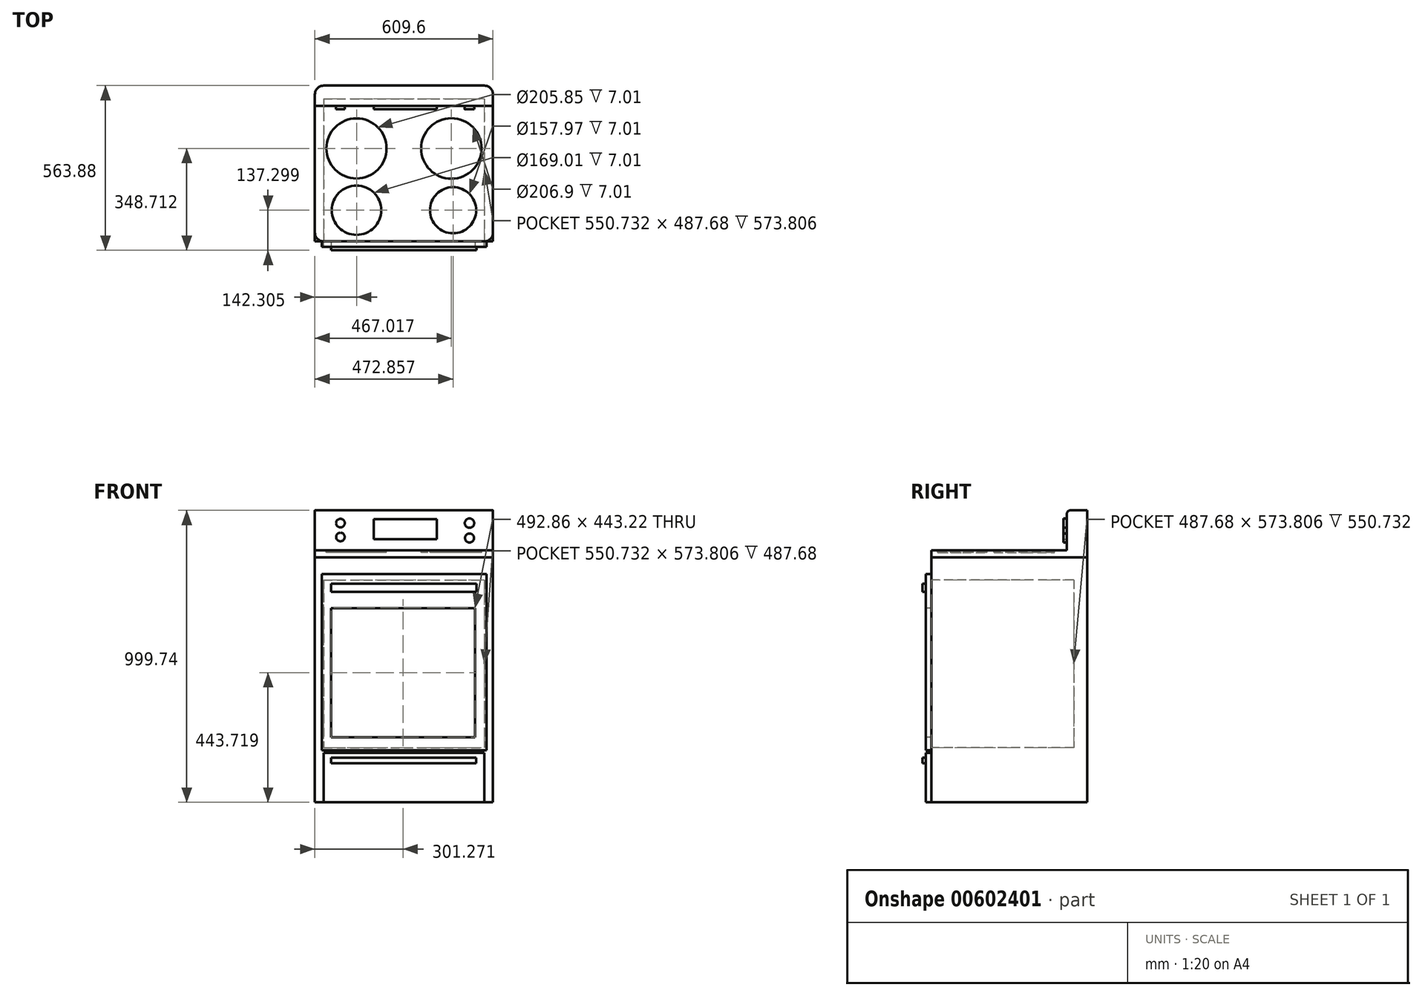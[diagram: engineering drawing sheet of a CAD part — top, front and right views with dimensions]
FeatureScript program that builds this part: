
annotation { "Feature Type Name" : "Feature", "Feature Type Description" : "" }
export const myFeature = defineFeature(function(context is Context, id is Id, definition is map)
    precondition{}
    {
        {
            var Q0;
            Q0=qCreatedBy(makeId("Top.planeOp"),FACE);
            var sketch = newSketch(context, id + "F0", { "sketchPlane" : qUnion([Q0])});
            skLineSegment(sketch, "E0.bottom", {"start": v(0, 0) * mm, "end": v(609.6, 0) * mm});
            skLineSegment(sketch, "E0.top", {"start": v(0, -533.4) * mm, "end": v(609.6, -533.4) * mm});
            skLineSegment(sketch, "E0.left", {"start": v(0, 0) * mm, "end": v(0, -533.4) * mm});
            skLineSegment(sketch, "E0.right", {"start": v(609.6, 0) * mm, "end": v(609.6, -533.4) * mm});
            skSolve(sketch);
        }
        {
            var Q0;
            Q0=makeQuery(id+"F0.imprint","IMPRINT",FACE,{"disambiguationData":[TD([[makeQuery(id+"F0.imprint","IMPRINT",EDGE,{"derivedFrom":sQuery(id+"F0.wireOp",EDGE,"E0.bottom")}),-1.0]])]});
            extrude(context, id + "F1", {"entities" : qUnion([Q0]), "depth" : 838.2 * mm, "offsetDistance" : 30.48 * mm});
        }
        {
            var Q0;
            Q0=makeQuery(id+"F1.opExtrude","CAP_FACE",FACE,{"disambiguationData":[OSD([sQuery(id+"F0.wireOp",EDGE,"E0.bottom"),sQuery(id+"F0.wireOp",EDGE,"E0.top"),sQuery(id+"F0.wireOp",EDGE,"E0.left"),sQuery(id+"F0.wireOp",EDGE,"E0.right")])],"isStart":false});
            var sketch = newSketch(context, id + "F2", { "sketchPlane" : qUnion([Q0])});
            skLineSegment(sketch, "E1.bottom", {"start": v(0, 0) * mm, "end": v(609.6, 0) * mm});
            skLineSegment(sketch, "E1.top", {"start": v(0, -533.4) * mm, "end": v(609.6, -533.4) * mm});
            skLineSegment(sketch, "E1.left", {"start": v(0, 0) * mm, "end": v(0, -533.4) * mm});
            skLineSegment(sketch, "E1.right", {"start": v(609.6, 0) * mm, "end": v(609.6, -533.4) * mm});
            skSolve(sketch);
        }
        {
            var Q0;
            Q0 = qSketchRegion(id + "F2", true);
            extrude(context, id + "F3", {"entities" : qUnion([Q0]), "depth" : 24.38 * mm, "offsetDistance" : 30.48 * mm});
        }
        {
            var Q0;
            Q0=makeQuery(id+"F3.opExtrude","SWEPT_EDGE",EDGE,{"disambiguationData":[OSD([sQuery(id+"F2.wireOp",EDGE,"E1.top"),sQuery(id+"F2.wireOp",EDGE,"E1.right")])]});
            var Q1;
            Q1=makeQuery(id+"F3.opExtrude","SWEPT_EDGE",EDGE,{"disambiguationData":[OSD([sQuery(id+"F2.wireOp",EDGE,"E1.top"),sQuery(id+"F2.wireOp",EDGE,"E1.left")])]});
            var Q2;
            Q2=makeQuery(id+"F3.opExtrude","SWEPT_EDGE",EDGE,{"disambiguationData":[OSD([sQuery(id+"F2.wireOp",EDGE,"E1.bottom"),sQuery(id+"F2.wireOp",EDGE,"E1.left")])]});
            var Q3;
            Q3=makeQuery(id+"F3.opExtrude","SWEPT_EDGE",EDGE,{"disambiguationData":[OSD([sQuery(id+"F2.wireOp",EDGE,"E1.bottom"),sQuery(id+"F2.wireOp",EDGE,"E1.right")])]});
            fillet(context, id + "F4", {"entities" : qUnion([Q0, Q1, Q2, Q3]), "radius" : 29.43 * mm, "tangentPropagation" : true, "allowEdgeOverflow" : false});
        }
        {
            var Q0;
            Q0=makeQuery(id+"F1.opExtrude","SWEPT_EDGE",EDGE,{"disambiguationData":[OSD([sQuery(id+"F0.wireOp",EDGE,"E0.bottom"),sQuery(id+"F0.wireOp",EDGE,"E0.right")])]});
            var Q1;
            Q1=makeQuery(id+"F1.opExtrude","SWEPT_EDGE",EDGE,{"disambiguationData":[OSD([sQuery(id+"F0.wireOp",EDGE,"E0.bottom"),sQuery(id+"F0.wireOp",EDGE,"E0.left")])]});
            fillet(context, id + "F5", {"entities" : qUnion([Q0, Q1]), "radius" : 29.43 * mm, "tangentPropagation" : true, "allowEdgeOverflow" : false});
        }
        {
            var Q0;
            Q0=makeQuery(id+"F3.opExtrude","CAP_FACE",FACE,{"disambiguationData":[OSD([sQuery(id+"F2.wireOp",EDGE,"E1.bottom"),sQuery(id+"F2.wireOp",EDGE,"E1.top"),sQuery(id+"F2.wireOp",EDGE,"E1.left"),sQuery(id+"F2.wireOp",EDGE,"E1.right")])],"isStart":false});
            var sketch = newSketch(context, id + "F6", { "sketchPlane" : qUnion([Q0])});
            skCircle(sketch, "E2", {"center": v(142.3, -426.58) * mm, "radius": 84.5 * mm});
            skCircle(sketch, "E3", {"center": v(472.86, -426.58) * mm, "radius": 78.99 * mm});
            skCircle(sketch, "E4", {"center": v(142.3, -215.17) * mm, "radius": 102.93 * mm});
            skCircle(sketch, "E5", {"center": v(467.02, -215.17) * mm, "radius": 103.45 * mm});
            skSolve(sketch);
        }
        {
            var Q0;
            Q0=makeQuery(id+"F6.imprint","IMPRINT",FACE,{"disambiguationData":[TD([[makeQuery(id+"F6.imprint","IMPRINT",EDGE,{"derivedFrom":sQuery(id+"F6.wireOp",EDGE,"E4")}),1.0]])]});
            var Q1;
            Q1=makeQuery(id+"F6.imprint","IMPRINT",FACE,{"disambiguationData":[TD([[makeQuery(id+"F6.imprint","IMPRINT",EDGE,{"derivedFrom":sQuery(id+"F6.wireOp",EDGE,"E5")}),1.0]])]});
            var Q2;
            Q2=makeQuery(id+"F6.imprint","IMPRINT",FACE,{"disambiguationData":[TD([[makeQuery(id+"F6.imprint","IMPRINT",EDGE,{"derivedFrom":sQuery(id+"F6.wireOp",EDGE,"E2")}),1.0]])]});
            var Q3;
            Q3=makeQuery(id+"F6.imprint","IMPRINT",FACE,{"disambiguationData":[TD([[makeQuery(id+"F6.imprint","IMPRINT",EDGE,{"derivedFrom":sQuery(id+"F6.wireOp",EDGE,"E3")}),1.0]])]});
            extrude(context, id + "F7", {"entities" : qUnion([Q0, Q1, Q2, Q3]), "operationType" : NewBodyOperationType.REMOVE, "oppositeDirection" : true, "depth" : 7 * mm, "offsetDistance" : 30.48 * mm});
        }
        {
            var Q0;
            Q0=makeQuery(id+"F1.opExtrude","SWEPT_FACE",FACE,{"disambiguationData":[OSD([sQuery(id+"F0.wireOp",EDGE,"E0.top")])]});
            var sketch = newSketch(context, id + "F8", { "sketchPlane" : qUnion([Q0])});
            skLineSegment(sketch, "E6.bottom", {"start": v(29.43, 169.25) * mm, "end": v(580.17, 169.25) * mm});
            skLineSegment(sketch, "E6.top", {"start": v(29.43, 0) * mm, "end": v(580.17, 0) * mm});
            skLineSegment(sketch, "E6.left", {"start": v(29.43, 169.25) * mm, "end": v(29.43, 0) * mm});
            skLineSegment(sketch, "E6.right", {"start": v(580.17, 169.25) * mm, "end": v(580.17, 0) * mm});
            skLineSegment(sketch, "E7.bottom", {"start": v(29.43, 761.04) * mm, "end": v(580.17, 761.04) * mm});
            skLineSegment(sketch, "E7.top", {"start": v(29.43, 187.23) * mm, "end": v(580.17, 187.23) * mm});
            skLineSegment(sketch, "E7.left", {"start": v(29.43, 761.04) * mm, "end": v(29.43, 187.23) * mm});
            skLineSegment(sketch, "E7.right", {"start": v(580.17, 761.04) * mm, "end": v(580.17, 187.23) * mm});
            skSolve(sketch);
        }
        {
            var Q0;
            Q0=makeQuery(id+"F8.imprint","IMPRINT",FACE,{"disambiguationData":[TD([[makeQuery(id+"F8.imprint","IMPRINT",EDGE,{"derivedFrom":sQuery(id+"F8.wireOp",EDGE,"E7.bottom")}),-1.0]])]});
            extrude(context, id + "F9", {"entities" : qUnion([Q0]), "operationType" : NewBodyOperationType.REMOVE, "oppositeDirection" : true, "depth" : 487.68 * mm, "offsetDistance" : 30.48 * mm});
        }
        {
            var Q0;
            Q0=makeQuery(id+"F8.imprint","IMPRINT",FACE,{"disambiguationData":[TD([[makeQuery(id+"F8.imprint","IMPRINT",EDGE,{"derivedFrom":sQuery(id+"F8.wireOp",EDGE,"E6.bottom")}),-1.0]])]});
            extrude(context, id + "F10", {"entities" : qUnion([Q0]), "operationType" : NewBodyOperationType.ADD, "depth" : 18.29 * mm, "offsetDistance" : 30.48 * mm});
        }
        {
            var Q0;
            Q0=makeQuery(id+"F8.imprint","IMPRINT",FACE,{"disambiguationData":[TD([[makeQuery(id+"F8.imprint","IMPRINT",EDGE,{"derivedFrom":sQuery(id+"F8.wireOp",EDGE,"E6.bottom")}),1.0]])]});
            var sketch = newSketch(context, id + "F11", { "sketchPlane" : qUnion([Q0])});
            skLineSegment(sketch, "E8.bottom", {"start": v(23.37, 780.98) * mm, "end": v(587.91, 780.98) * mm});
            skLineSegment(sketch, "E8.top", {"start": v(23.37, 178.25) * mm, "end": v(587.91, 178.25) * mm});
            skLineSegment(sketch, "E8.left", {"start": v(23.37, 780.98) * mm, "end": v(23.37, 178.25) * mm});
            skLineSegment(sketch, "E8.right", {"start": v(587.91, 780.98) * mm, "end": v(587.91, 178.25) * mm});
            skSolve(sketch);
        }
        {
            var Q0;
            Q0 = qSketchRegion(id + "F11", true);
            extrude(context, id + "F12", {"entities" : qUnion([Q0]), "operationType" : NewBodyOperationType.ADD, "depth" : 18.29 * mm, "offsetDistance" : 30.48 * mm});
        }
        {
            var Q0;
            Q0=makeQuery(id+"F12.opExtrude","CAP_FACE",FACE,{"disambiguationData":[OSD([sQuery(id+"F11.wireOp",EDGE,"E8.bottom"),sQuery(id+"F11.wireOp",EDGE,"E8.top"),sQuery(id+"F11.wireOp",EDGE,"E8.left"),sQuery(id+"F11.wireOp",EDGE,"E8.right")])],"isStart":false});
            var sketch = newSketch(context, id + "F13", { "sketchPlane" : qUnion([Q0])});
            skLineSegment(sketch, "E9.bottom", {"start": v(54.84, 748.66) * mm, "end": v(553.02, 748.66) * mm});
            skLineSegment(sketch, "E9.top", {"start": v(54.84, 720.29) * mm, "end": v(553.02, 720.29) * mm});
            skLineSegment(sketch, "E9.left", {"start": v(54.84, 748.66) * mm, "end": v(54.84, 720.29) * mm});
            skLineSegment(sketch, "E9.right", {"start": v(553.02, 748.66) * mm, "end": v(553.02, 720.29) * mm});
            skSolve(sketch);
        }
        {
            var Q0;
            Q0=makeQuery(id+"F13.imprint","IMPRINT",FACE,{"disambiguationData":[TD([[makeQuery(id+"F13.imprint","IMPRINT",EDGE,{"derivedFrom":sQuery(id+"F13.wireOp",EDGE,"E9.bottom")}),-1.0]])]});
            extrude(context, id + "F14", {"entities" : qUnion([Q0]), "operationType" : NewBodyOperationType.ADD, "depth" : 12.2 * mm, "offsetDistance" : 30.48 * mm});
        }
        {
            var Q0;
            Q0=makeQuery(id+"F12.opExtrude","CAP_FACE",FACE,{"disambiguationData":[OSD([sQuery(id+"F11.wireOp",EDGE,"E8.bottom"),sQuery(id+"F11.wireOp",EDGE,"E8.top"),sQuery(id+"F11.wireOp",EDGE,"E8.left"),sQuery(id+"F11.wireOp",EDGE,"E8.right")])],"isStart":false});
            var sketch = newSketch(context, id + "F15", { "sketchPlane" : qUnion([Q0])});
            skLineSegment(sketch, "E10.bottom", {"start": v(54.84, 665.33) * mm, "end": v(547.7, 665.33) * mm});
            skLineSegment(sketch, "E10.top", {"start": v(54.84, 222.1) * mm, "end": v(547.7, 222.1) * mm});
            skLineSegment(sketch, "E10.left", {"start": v(54.84, 665.33) * mm, "end": v(54.84, 222.1) * mm});
            skLineSegment(sketch, "E10.right", {"start": v(547.7, 665.33) * mm, "end": v(547.7, 222.1) * mm});
            skSolve(sketch);
        }
        {
            var Q0;
            Q0=makeQuery(id+"F15.imprint","IMPRINT",FACE,{"disambiguationData":[TD([[makeQuery(id+"F15.imprint","IMPRINT",EDGE,{"derivedFrom":sQuery(id+"F15.wireOp",EDGE,"E10.bottom")}),-1.0]])]});
            extrude(context, id + "F16", {"entities" : qUnion([Q0]), "operationType" : NewBodyOperationType.REMOVE, "oppositeDirection" : true, "depth" : 70.1 * mm, "offsetDistance" : 30.48 * mm});
        }
        {
            var Q0;
            Q0=makeQuery(id+"F10.opExtrude","CAP_FACE",FACE,{"disambiguationData":[OSD([sQuery(id+"F8.wireOp",EDGE,"E6.bottom"),sQuery(id+"F8.wireOp",EDGE,"E6.top"),sQuery(id+"F8.wireOp",EDGE,"E6.left"),sQuery(id+"F8.wireOp",EDGE,"E6.right")])],"isStart":false});
            var sketch = newSketch(context, id + "F17", { "sketchPlane" : qUnion([Q0])});
            skLineSegment(sketch, "E11.bottom", {"start": v(54.84, 152.97) * mm, "end": v(551.25, 152.97) * mm});
            skLineSegment(sketch, "E11.top", {"start": v(54.84, 133.46) * mm, "end": v(551.25, 133.46) * mm});
            skLineSegment(sketch, "E11.left", {"start": v(54.84, 152.97) * mm, "end": v(54.84, 133.46) * mm});
            skLineSegment(sketch, "E11.right", {"start": v(551.25, 152.97) * mm, "end": v(551.25, 133.46) * mm});
            skSolve(sketch);
        }
        {
            var Q0;
            Q0=makeQuery(id+"F17.imprint","IMPRINT",FACE,{"disambiguationData":[TD([[makeQuery(id+"F17.imprint","IMPRINT",EDGE,{"derivedFrom":sQuery(id+"F17.wireOp",EDGE,"E11.bottom")}),-1.0]])]});
            extrude(context, id + "F18", {"entities" : qUnion([Q0]), "operationType" : NewBodyOperationType.ADD, "depth" : 12.2 * mm, "offsetDistance" : 30.48 * mm});
        }
        {
            var Q0;
            Q0=makeQuery(id+"F3.opExtrude","CAP_FACE",FACE,{"disambiguationData":[OSD([sQuery(id+"F2.wireOp",EDGE,"E1.bottom"),sQuery(id+"F2.wireOp",EDGE,"E1.top"),sQuery(id+"F2.wireOp",EDGE,"E1.left"),sQuery(id+"F2.wireOp",EDGE,"E1.right")])],"isStart":false});
            var sketch = newSketch(context, id + "F19", { "sketchPlane" : qUnion([Q0])});
            skLineSegment(sketch, "E12.bottom", {"start": v(0, 0) * mm, "end": v(609.6, 0) * mm});
            skLineSegment(sketch, "E12.top", {"start": v(0, -69.17) * mm, "end": v(609.6, -69.17) * mm});
            skLineSegment(sketch, "E12.left", {"start": v(0, 0) * mm, "end": v(0, -69.17) * mm});
            skLineSegment(sketch, "E12.right", {"start": v(609.6, 0) * mm, "end": v(609.6, -69.17) * mm});
            skSolve(sketch);
        }
        {
            var Q0;
            {var subQ6=sQuery(id+"F19.wireOp",EDGE,"E12.top");Q0=makeQuery(id+"F19.imprint","IMPRINT",FACE,{"disambiguationData":[TD([[makeQuery(id+"F19.imprint","IMPRINT",EDGE,{"derivedFrom":subQ6}),1.0]])]});}
            extrude(context, id + "F20", {"entities" : qUnion([Q0]), "operationType" : NewBodyOperationType.ADD, "depth" : 137.16 * mm, "offsetDistance" : 30.48 * mm});
        }
        {
            var Q0;
            Q0=makeQuery(id+"F20.opExtrude","CAP_EDGE",EDGE,{"disambiguationData":[OSD([sQuery(id+"F19.wireOp",EDGE,"E12.top")])],"isStart":false});
            fillet(context, id + "F21", {"entities" : qUnion([Q0]), "radius" : 11.77 * mm, "tangentPropagation" : true, "allowEdgeOverflow" : false});
        }
        {
            var Q0;
            Q0=makeQuery(id+"F20.opExtrude","SWEPT_FACE",FACE,{"disambiguationData":[OSD([sQuery(id+"F19.wireOp",EDGE,"E12.top")])]});
            var sketch = newSketch(context, id + "F22", { "sketchPlane" : qUnion([Q0])});
            skLineSegment(sketch, "E13.bottom", {"start": v(201.48, 969.48) * mm, "end": v(417, 969.48) * mm});
            skLineSegment(sketch, "E13.top", {"start": v(201.48, 900.52) * mm, "end": v(417, 900.52) * mm});
            skLineSegment(sketch, "E13.left", {"start": v(201.48, 969.48) * mm, "end": v(201.48, 900.52) * mm});
            skLineSegment(sketch, "E13.right", {"start": v(417, 969.48) * mm, "end": v(417, 900.52) * mm});
            skCircle(sketch, "E14", {"center": v(529.06, 955.83) * mm, "radius": 16.06 * mm});
            skCircle(sketch, "E15", {"center": v(529.06, 904.83) * mm, "radius": 15.27 * mm});
            skCircle(sketch, "E16", {"center": v(87.25, 955.83) * mm, "radius": 14.8 * mm});
            skCircle(sketch, "E17", {"center": v(87.25, 908.42) * mm, "radius": 14.74 * mm});
            skSolve(sketch);
        }
        {
            var Q0;
            Q0=makeQuery(id+"F22.imprint","IMPRINT",FACE,{"disambiguationData":[TD([[makeQuery(id+"F22.imprint","IMPRINT",EDGE,{"derivedFrom":sQuery(id+"F22.wireOp",EDGE,"E16")}),1.0]])]});
            var Q1;
            Q1=makeQuery(id+"F22.imprint","IMPRINT",FACE,{"disambiguationData":[TD([[makeQuery(id+"F22.imprint","IMPRINT",EDGE,{"derivedFrom":sQuery(id+"F22.wireOp",EDGE,"E17")}),1.0]])]});
            var Q2;
            Q2=makeQuery(id+"F22.imprint","IMPRINT",FACE,{"disambiguationData":[TD([[makeQuery(id+"F22.imprint","IMPRINT",EDGE,{"derivedFrom":sQuery(id+"F22.wireOp",EDGE,"E13.bottom")}),-1.0]])]});
            var Q3;
            Q3=makeQuery(id+"F22.imprint","IMPRINT",FACE,{"disambiguationData":[TD([[makeQuery(id+"F22.imprint","IMPRINT",EDGE,{"derivedFrom":sQuery(id+"F22.wireOp",EDGE,"E14")}),1.0]])]});
            var Q4;
            Q4=makeQuery(id+"F22.imprint","IMPRINT",FACE,{"disambiguationData":[TD([[makeQuery(id+"F22.imprint","IMPRINT",EDGE,{"derivedFrom":sQuery(id+"F22.wireOp",EDGE,"E15")}),1.0]])]});
            extrude(context, id + "F23", {"entities" : qUnion([Q0, Q1, Q2, Q3, Q4]), "operationType" : NewBodyOperationType.ADD, "depth" : 12.2 * mm, "offsetDistance" : 30.48 * mm});
        }
    });
